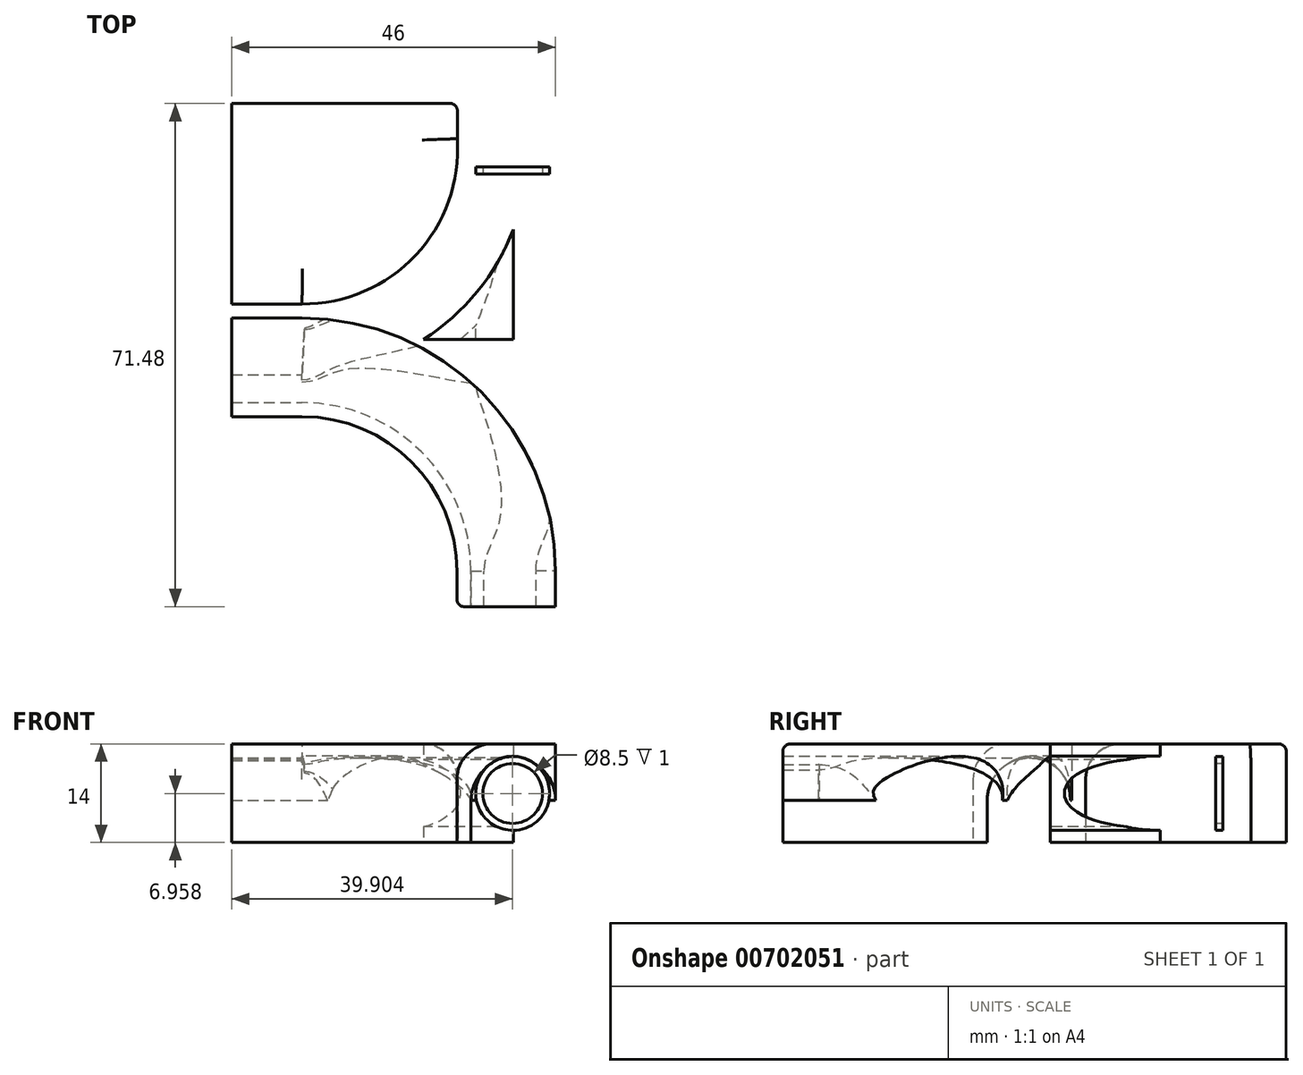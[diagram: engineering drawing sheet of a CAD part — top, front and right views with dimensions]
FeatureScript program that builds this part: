
annotation { "Feature Type Name" : "Feature", "Feature Type Description" : "" }
export const myFeature = defineFeature(function(context is Context, id is Id, definition is map)
    precondition{}
    {
        {
            var Q0;
            Q0=qCreatedBy(makeId("Top.planeOp"),FACE);
            var sketch = newSketch(context, id + "F0", { "sketchPlane" : qUnion([Q0])});
            skArc(sketch, "E0", {"start": v(30, 0) * mm, "mid": v(21.25, 21.18) * mm, "end": v(0.1, 30) * mm});
            skLineSegment(sketch, "E1", {"start": v(0.1, 30) * mm, "end": v(30.06, 30) * mm, "construction": true});
            skLineSegment(sketch, "E2", {"start": v(30.06, 1.48) * mm, "end": v(30.06, 61.48) * mm});
            skArc(sketch, "E3", {"start": v(0.1, 30) * mm, "mid": v(21.83, 39.32) * mm, "end": v(30.06, 61.48) * mm});
            skLineSegment(sketch, "E4", {"start": v(30, 0) * mm, "end": v(30, -1.64) * mm});
            skSolve(sketch);
        }
        {
            var Q0;
            Q0=qCreatedBy(makeId("Top.planeOp"),FACE);
            var sketch = newSketch(context, id + "F1", { "sketchPlane" : qUnion([Q0])});
            skLineSegment(sketch, "E5.bottom", {"start": v(0, 0) * mm, "end": v(37.06, 0) * mm});
            skLineSegment(sketch, "E5.top", {"start": v(0, 61.48) * mm, "end": v(37.06, 61.48) * mm});
            skLineSegment(sketch, "E5.left", {"start": v(0, 0) * mm, "end": v(0, 61.48) * mm});
            skLineSegment(sketch, "E5.right", {"start": v(37.06, 0) * mm, "end": v(37.06, 61.48) * mm});
            skSolve(sketch);
        }
        {
            var Q0;
            Q0=makeQuery(id+"F1.imprint","IMPRINT",FACE,{"disambiguationData":[TD([[makeQuery(id+"F1.imprint","IMPRINT",EDGE,{"derivedFrom":sQuery(id+"F1.wireOp",EDGE,"E5.bottom")}),1.0]])]});
            extrude(context, id + "F2", {"entities" : qUnion([Q0]), "depth" : 14 * mm, "offsetDistance" : 25 * mm});
        }
        {
            var Q0;
            Q0=makeQuery(id+"F2.opExtrude","SWEPT_FACE",FACE,{"disambiguationData":[OSD([sQuery(id+"F1.wireOp",EDGE,"E5.left")])]});
            var sketch = newSketch(context, id + "F3", { "sketchPlane" : qUnion([Q0])});
            skLineSegment(sketch, "E6", {"start": v(-36, 0) * mm, "end": v(-24, 0) * mm});
            skLineSegment(sketch, "E7", {"start": v(-30, 0) * mm, "end": v(-30, 6) * mm, "construction": true});
            skArc(sketch, "E8", {"start": v(-24, 6) * mm, "mid": v(-30, 12) * mm, "end": v(-36, 6) * mm});
            skLineSegment(sketch, "E9", {"start": v(-36, 0) * mm, "end": v(-36, 6) * mm});
            skLineSegment(sketch, "E10", {"start": v(-24, 0) * mm, "end": v(-24, 6) * mm});
            skSolve(sketch);
        }
        {
            var Q0;
            Q0=makeQuery(id+"F3.imprint","IMPRINT",FACE,{"disambiguationData":[TD([[makeQuery(id+"F3.imprint","IMPRINT",EDGE,{"derivedFrom":sQuery(id+"F3.wireOp",EDGE,"E6")}),-1.0]])]});
            var Q1;
            Q1=sQuery(id+"F0.wireOp",EDGE,"E0");
            var Q2;
            Q2=sQuery(id+"F0.wireOp",EDGE,"E4");
            sweep(context, id + "F4", {"operationType" : NewBodyOperationType.REMOVE, "profiles" : qUnion([Q0]), "path" : qUnion([Q1, Q2])});
        }
        {
            var Q0;
            Q0=makeQuery(id+"F2.opExtrude","SWEPT_FACE",FACE,{"disambiguationData":[OSD([sQuery(id+"F1.wireOp",EDGE,"E5.top")])]});
            var sketch = newSketch(context, id + "F5", { "sketchPlane" : qUnion([Q0])});
            skCircle(sketch, "E11", {"center": v(-29.9, 7) * mm, "radius": 5.25 * mm});
            skLineSegment(sketch, "E12", {"start": v(-29.9, 0) * mm, "end": v(-29.9, 7.97) * mm, "construction": true});
            skSolve(sketch);
        }
        {
            var Q0;
            Q0=makeQuery(id+"F5.imprint","IMPRINT",FACE,{"disambiguationData":[TD([[makeQuery(id+"F5.imprint","IMPRINT",EDGE,{"derivedFrom":sQuery(id+"F5.wireOp",EDGE,"E11")}),1.0]])]});
            extrude(context, id + "F6", {"entities" : qUnion([Q0]), "operationType" : NewBodyOperationType.REMOVE, "endBound" : BoundingType.THROUGH_ALL, "oppositeDirection" : true, "depth" : 25 * mm, "offsetDistance" : 25 * mm});
        }
        {
            var Q0;
            Q0=makeQuery(id+"F2.opExtrude","SWEPT_FACE",FACE,{"disambiguationData":[OSD([sQuery(id+"F1.wireOp",EDGE,"E5.top")])]});
            var sketch = newSketch(context, id + "F7", { "sketchPlane" : qUnion([Q0])});
            skCircle(sketch, "E13", {"center": v(-29.9, 7) * mm, "radius": 5.25 * mm});
            skSolve(sketch);
        }
        {
            var Q0;
            Q0=makeQuery(id+"F7.imprint","IMPRINT",FACE,{"disambiguationData":[TD([[makeQuery(id+"F7.imprint","IMPRINT",EDGE,{"derivedFrom":sQuery(id+"F7.wireOp",EDGE,"E13")}),1.0]])]});
            var Q1;
            Q1=sQuery(id+"F7.wireOp",EDGE,"E13");
            var Q2;
            Q2=sQuery(id+"F0.wireOp",EDGE,"E3");
            sweep(context, id + "F8", {"operationType" : NewBodyOperationType.REMOVE, "profiles" : qUnion([Q0]), "surfaceProfiles" : qUnion([Q1]), "path" : qUnion([Q2])});
        }
        {
            var Q0;
            {var subQ0=sQuery(id+"F1.wireOp",EDGE,"E5.left");var subQ1=sQuery(id+"F1.wireOp",EDGE,"E5.top");var subQ2=sQuery(id+"F1.wireOp",EDGE,"E5.right");var subQ4=sQuery(id+"F1.wireOp",EDGE,"E5.bottom");Q0=makeQuery(id+"F4.boolean.opBoolean","SPLIT",FACE,{"disambiguationData":[TD([makeQuery(id+"F2.opExtrude","SWEPT_FACE",FACE,{"disambiguationData":[OSD([subQ1])]})])],"derivedFrom":makeQuery(id+"F2.opExtrude","CAP_FACE",FACE,{"disambiguationData":[OSD([subQ4,subQ1,subQ0,subQ2])],"isStart":true})});}
            var sketch = newSketch(context, id + "F9", { "sketchPlane" : qUnion([Q0])});
            skArc(sketch, "E14.0", {"start": v(0, -38) * mm, "mid": v(16.14, -44.94) * mm, "end": v(22.05, -61.48) * mm});
            skLineSegment(sketch, "E15", {"start": v(0, -38) * mm, "end": v(0, -61.48) * mm});
            skLineSegment(sketch, "E16", {"start": v(0, -61.48) * mm, "end": v(22.05, -61.48) * mm});
            skArc(sketch, "E17.0", {"start": v(0, -22) * mm, "mid": v(15.56, -15.56) * mm, "end": v(22, 0) * mm});
            skLineSegment(sketch, "E18", {"start": v(22, 0) * mm, "end": v(0, 0) * mm});
            skLineSegment(sketch, "E19", {"start": v(0, -22) * mm, "end": v(0, 0) * mm});
            skArc(sketch, "E20.0", {"start": v(17.23, -32.97) * mm, "mid": v(24.88, -39.75) * mm, "end": v(30, -48.6) * mm});
            skLineSegment(sketch, "E21", {"start": v(30, -48.6) * mm, "end": v(30, -32.97) * mm});
            skLineSegment(sketch, "E22", {"start": v(30, -32.97) * mm, "end": v(17.23, -32.97) * mm});
            skSolve(sketch);
        }
        {
            var Q0;
            Q0=makeQuery(id+"F9.imprint","IMPRINT",FACE,{"disambiguationData":[TD([[makeQuery(id+"F9.imprint","IMPRINT",EDGE,{"derivedFrom":sQuery(id+"F9.wireOp",EDGE,"E14.0")}),-1.0]])]});
            var Q1;
            Q1=makeQuery(id+"F9.imprint","IMPRINT",FACE,{"disambiguationData":[TD([[makeQuery(id+"F9.imprint","IMPRINT",EDGE,{"derivedFrom":sQuery(id+"F9.wireOp",EDGE,"E17.0")}),1.0]])]});
            extrude(context, id + "F10", {"entities" : qUnion([Q0, Q1]), "operationType" : NewBodyOperationType.REMOVE, "endBound" : BoundingType.THROUGH_ALL, "oppositeDirection" : true, "depth" : 25 * mm, "offsetDistance" : 25 * mm});
        }
        {
            var Q0;
            {var subQ0=sQuery(id+"F3.wireOp",EDGE,"E8");var subQ3=sQuery(id+"F0.wireOp",EDGE,"E0");Q0=makeQuery(id+"F8.boolean.opBoolean","INTERSECT",EDGE,{"disambiguationData":[OD(1.0)],"derivedFrom":[makeQuery(id+"F6.boolean.opBoolean","SPLIT",FACE,{"disambiguationData":[TD([makeQuery(id+"F2.opExtrude","SWEPT_FACE",FACE,{"disambiguationData":[OSD([sQuery(id+"F1.wireOp",EDGE,"E5.left")])]})])],"derivedFrom":makeQuery(id+"F4.boolean.opBoolean","COPY",FACE,{"derivedFrom":makeQuery(id+"F4.opSweep","SWEPT_FACE",FACE,{"disambiguationData":[OSD([subQ3,subQ0])]})})}),makeQuery(id+"F8.opSweep","SWEPT_FACE",FACE,{"disambiguationData":[OSD([sQuery(id+"F0.wireOp",EDGE,"E3"),sQuery(id+"F7.wireOp",EDGE,"E13")])]})]});}
            fillet(context, id + "F11", {"entities" : qUnion([Q0]), "radius" : 5 * mm, "tangentPropagation" : true, "allowEdgeOverflow" : false});
        }
        {
            var Q0;
            Q0=makeQuery(id+"F2.opExtrude","SWEPT_FACE",FACE,{"disambiguationData":[OSD([sQuery(id+"F1.wireOp",EDGE,"E5.top")])]});
            extrude(context, id + "F12", {"entities" : qUnion([Q0]), "operationType" : NewBodyOperationType.ADD, "depth" : 5 * mm, "offsetDistance" : 25 * mm});
        }
        {
            var Q0;
            Q0=makeQuery(id+"F12.opExtrude","CAP_FACE",FACE,{"disambiguationData":[OSD([sQuery(id+"F1.wireOp",EDGE,"E5.top")])],"isStart":false});
            cPlane(context, id + "F13", {"entities" : qUnion([Q0]), "cplaneType" : CPlaneType.OFFSET, "offset" : 10 * mm, "oppositeDirection" : true, "width" : 150 * mm, "height" : 150 * mm});
        }
        {
            var Q0;
            Q0=qCreatedBy(id+"F13.planeOp",FACE);
            var sketch = newSketch(context, id + "F14", { "sketchPlane" : qUnion([Q0])});
            skCircle(sketch, "E23", {"center": v(-29.9, 6.96) * mm, "radius": 5.25 * mm});
            skCircle(sketch, "E24.0", {"center": v(-29.9, 6.96) * mm, "radius": 4.25 * mm});
            skSolve(sketch);
        }
        {
            var Q0;
            Q0=makeQuery(id+"F14.imprint","IMPRINT",FACE,{"disambiguationData":[TD([[makeQuery(id+"F14.imprint","IMPRINT",EDGE,{"derivedFrom":sQuery(id+"F14.wireOp",EDGE,"E23")}),1.0]])]});
            extrude(context, id + "F15", {"entities" : qUnion([Q0]), "operationType" : NewBodyOperationType.ADD, "depth" : 1 * mm, "offsetDistance" : 25 * mm});
        }
        {
            var Q0;
            Q0=makeQuery(id+"F2.opExtrude","SWEPT_FACE",FACE,{"disambiguationData":[OSD([sQuery(id+"F1.wireOp",EDGE,"E5.left")])]});
            extrude(context, id + "F16", {"entities" : qUnion([Q0]), "operationType" : NewBodyOperationType.ADD, "depth" : 10 * mm, "offsetDistance" : 25 * mm});
        }
        {
            var Q0;
            Q0=makeQuery(id+"F2.opExtrude","SWEPT_FACE",FACE,{"disambiguationData":[OSD([sQuery(id+"F1.wireOp",EDGE,"E5.bottom")])]});
            extrude(context, id + "F17", {"entities" : qUnion([Q0]), "operationType" : NewBodyOperationType.ADD, "depth" : 5 * mm, "offsetDistance" : 25 * mm});
        }
        {
            var Q0;
            Q0=makeQuery(id+"F10.boolean.opBoolean","INTERSECT",EDGE,{"derivedFrom":[makeQuery(id+"F2.opExtrude","CAP_FACE",FACE,{"disambiguationData":[OSD([sQuery(id+"F1.wireOp",EDGE,"E5.bottom"),sQuery(id+"F1.wireOp",EDGE,"E5.top"),sQuery(id+"F1.wireOp",EDGE,"E5.left"),sQuery(id+"F1.wireOp",EDGE,"E5.right")])],"isStart":false}),makeQuery(id+"F10.opExtrude","SWEPT_FACE",FACE,{"disambiguationData":[OSD([sQuery(id+"F9.wireOp",EDGE,"E14.0")])]})]});
            var Q1;
            Q1=makeQuery(id+"F16.opExtrude","SWEPT_EDGE",EDGE,{"disambiguationData":[OSD([sQuery(id+"F1.wireOp",EDGE,"E5.bottom"),sQuery(id+"F1.wireOp",EDGE,"E5.top"),sQuery(id+"F1.wireOp",EDGE,"E5.left"),sQuery(id+"F1.wireOp",EDGE,"E5.right"),sQuery(id+"F9.wireOp",EDGE,"E14.0")])]});
            var Q2;
            Q2=makeQuery(id+"F16.opExtrude","SWEPT_EDGE",EDGE,{"disambiguationData":[OSD([sQuery(id+"F1.wireOp",EDGE,"E5.bottom"),sQuery(id+"F1.wireOp",EDGE,"E5.top"),sQuery(id+"F1.wireOp",EDGE,"E5.left"),sQuery(id+"F1.wireOp",EDGE,"E5.right"),sQuery(id+"F9.wireOp",EDGE,"E17.0")])]});
            var Q3;
            {var subQ0=sQuery(id+"F1.wireOp",EDGE,"E5.right");var subQ1=sQuery(id+"F1.wireOp",EDGE,"E5.bottom");var subQ2=sQuery(id+"F1.wireOp",EDGE,"E5.top");Q3=makeQuery(id+"F17.boolean.opBoolean","MERGE",EDGE,{"derivedFrom":[makeQuery(id+"F12.boolean.opBoolean","MERGE",EDGE,{"derivedFrom":[makeQuery(id+"F2.opExtrude","CAP_EDGE",EDGE,{"disambiguationData":[OSD([subQ0])],"isStart":false}),makeQuery(id+"F12.opExtrude","SWEPT_EDGE",EDGE,{"disambiguationData":[OSD([subQ2,subQ0]),TDD([makeQuery(id+"F2.opExtrude","CAP_VERTEX",VERTEX,{"disambiguationData":[OSD([subQ2,subQ0])],"isStart":false})])]})]}),makeQuery(id+"F17.opExtrude","SWEPT_EDGE",EDGE,{"disambiguationData":[OSD([subQ1,subQ0]),TDD([makeQuery(id+"F2.opExtrude","CAP_VERTEX",VERTEX,{"disambiguationData":[OSD([subQ1,subQ0])],"isStart":false})])]})]});}
            fillet(context, id + "F18", {"entities" : qUnion([Q0, Q1, Q2, Q3]), "radius" : 5 * mm, "tangentPropagation" : true, "allowEdgeOverflow" : false});
        }
        {
            var Q0;
            {var subQ0=sQuery(id+"F1.wireOp",EDGE,"E5.top");Q0=makeQuery(id+"F18.opFillet","BLEND_EDGE",EDGE,{"blendedFrom":[makeQuery(id+"F10.boolean.opBoolean","INTERSECT",EDGE,{"derivedFrom":[makeQuery(id+"F2.opExtrude","CAP_FACE",FACE,{"disambiguationData":[OSD([sQuery(id+"F1.wireOp",EDGE,"E5.bottom"),subQ0,sQuery(id+"F1.wireOp",EDGE,"E5.left"),sQuery(id+"F1.wireOp",EDGE,"E5.right")])],"isStart":false}),makeQuery(id+"F10.opExtrude","SWEPT_FACE",FACE,{"disambiguationData":[OSD([sQuery(id+"F9.wireOp",EDGE,"E14.0")])]})]}),makeQuery(id+"F12.opExtrude","CAP_FACE",FACE,{"disambiguationData":[OSD([subQ0])],"isStart":false})],"blendedInto":[makeQuery(id+"F12.opExtrude","CAP_FACE",FACE,{"disambiguationData":[OSD([subQ0])],"isStart":false})]});}
            var Q1;
            Q1=makeQuery(id+"F12.opExtrude","CAP_EDGE",EDGE,{"disambiguationData":[OSD([sQuery(id+"F1.wireOp",EDGE,"E5.top"),sQuery(id+"F9.wireOp",EDGE,"E14.0"),sQuery(id+"F9.wireOp",EDGE,"E16")])],"isStart":false});
            var Q2;
            Q2=makeQuery(id+"F17.opExtrude","CAP_EDGE",EDGE,{"disambiguationData":[OSD([sQuery(id+"F9.wireOp",EDGE,"E17.0"),sQuery(id+"F9.wireOp",EDGE,"E18")])],"isStart":false});
            fillet(context, id + "F19", {"entities" : qUnion([Q0, Q1, Q2]), "radius" : 1 * mm, "tangentPropagation" : true, "allowEdgeOverflow" : false});
        }
    });
